# Revit family: Esserbus transponder
name_source: partatom
category: Fire Alarm Devices
revit_build: Autodesk Revit 2014 (Build: 20130308_1515(x64)
units: mm (PartAtom-declared; Revit-internal decimal feet)

## types (5) — shared parameters
Manufacturer = Esser by Honeywell
URL = http://www.esser-systems.com
b1 = 20 mm  [stored 0.0656168 ft]
content_date_modified = 16.06.2015
content_version = 1.0
material = White
material 2 = Black

## per-type parameters (varying)
| type | Model | article number | h1 | l1 |
| esserbus alarm transponder | esserbus alarm transponder, 4 IN/2 OUT with isolator | 808623 | 72 mm  [stored 0.23622 ft] | 82 mm  [stored 0.269029 ft] |
| esserbus transponder 12 relays (8 bit) | esserbus transponder 12 relays (8 bit) | 808610.1 | 82 mm  [stored 0.269029 ft] | 150 mm |
| esserbus transponder 32 LED | esserbus transponder 32 LED | 808611.1 | 82 mm  [stored 0.269029 ft] | 150 mm |
| esserbus transponder for UniVario | esserbus transponder for UniVario with isolator | 808623.1 | 82 mm  [stored 0.269029 ft] | 150 mm |
| esserbus FSA transponder for fire doors | esserbus FSA transponder for fire doors | 808619.1 | 82 mm  [stored 0.269029 ft] | 150 mm |

note: [stored X ft] marks values corroborated as IEEE doubles in the binary element streams (Revit-internal decimal feet)

## geometry (parser evidence)
native form markers: Sweep x4
no freeform markers — native parametric forms only
